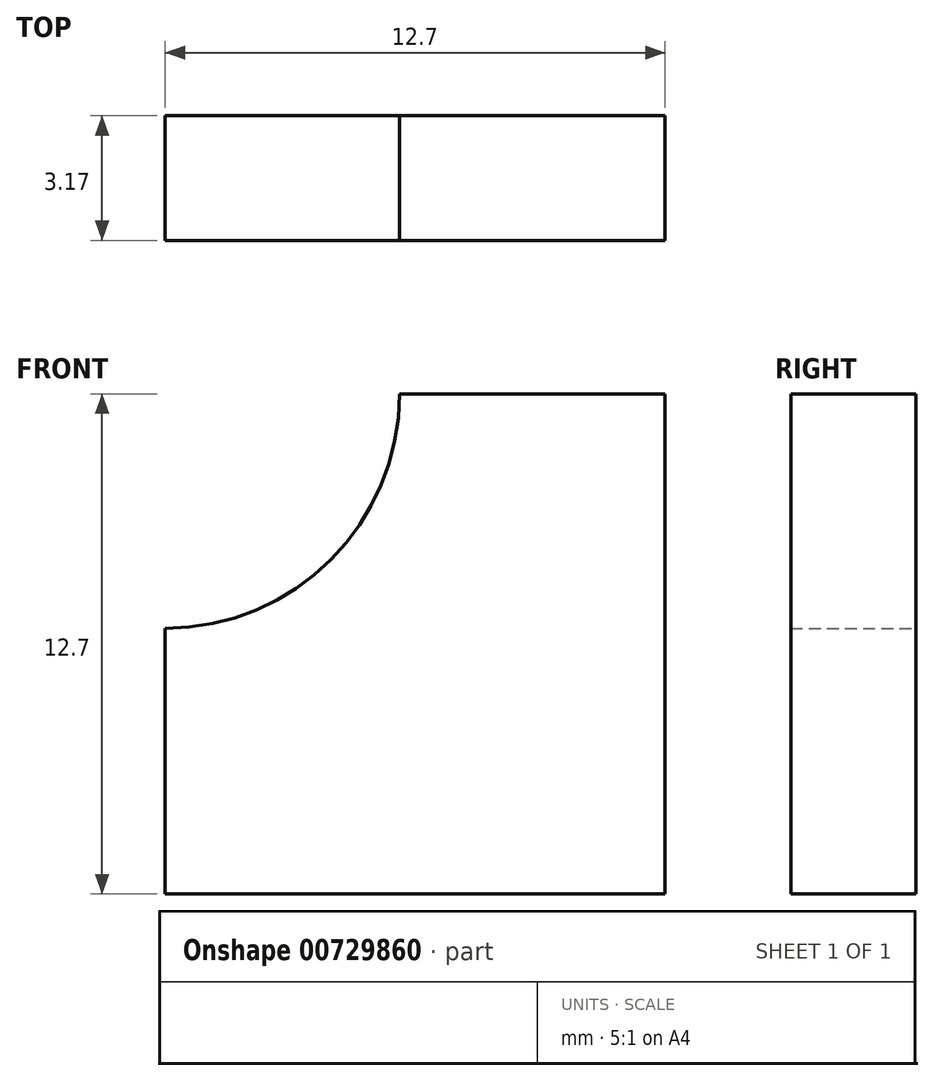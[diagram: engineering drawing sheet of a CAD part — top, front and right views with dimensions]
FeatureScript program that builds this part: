
annotation { "Feature Type Name" : "Feature", "Feature Type Description" : "" }
export const myFeature = defineFeature(function(context is Context, id is Id, definition is map)
    precondition{}
    {
        {
            var Q0;
            Q0=qCreatedBy(makeId("Front.planeOp"),FACE);
            var sketch = newSketch(context, id + "F0", { "sketchPlane" : qUnion([Q0])});
            skLineSegment(sketch, "E0.bottom", {"start": v(-37.74, 10.23) * mm, "end": v(-12.34, 10.23) * mm});
            skLineSegment(sketch, "E0.top", {"start": v(-37.74, -15.17) * mm, "end": v(-12.34, -15.17) * mm});
            skLineSegment(sketch, "E0.left", {"start": v(-37.74, 10.23) * mm, "end": v(-37.74, -15.17) * mm});
            skLineSegment(sketch, "E0.right", {"start": v(-12.34, 10.23) * mm, "end": v(-12.34, -15.17) * mm});
            skLineSegment(sketch, "E1.bottom", {"start": v(-25.04, 10.23) * mm, "end": v(-12.34, 10.23) * mm});
            skLineSegment(sketch, "E1.top", {"start": v(-25.04, -15.17) * mm, "end": v(-12.34, -15.17) * mm});
            skLineSegment(sketch, "E1.left", {"start": v(-25.04, 10.23) * mm, "end": v(-25.04, -15.17) * mm});
            skLineSegment(sketch, "E2.bottom", {"start": v(-12.34, 10.23) * mm, "end": v(-37.74, 10.23) * mm});
            skLineSegment(sketch, "E2.top", {"start": v(-12.34, -2.47) * mm, "end": v(-37.74, -2.47) * mm});
            skLineSegment(sketch, "E2.left", {"start": v(-12.34, 10.23) * mm, "end": v(-12.34, -2.47) * mm});
            skLineSegment(sketch, "E2.right", {"start": v(-37.74, 10.23) * mm, "end": v(-37.74, -2.47) * mm});
            skCircle(sketch, "E3", {"center": v(-25.04, -2.47) * mm, "radius": 5.95 * mm});
            skCircle(sketch, "E4", {"center": v(-31, -2.47) * mm, "radius": 3.97 * mm});
            skSolve(sketch);
        }
        {
            var Q0;
            {var subQ0=sQuery(id+"F0.wireOp",EDGE,"E2.right");Q0=makeQuery(id+"F0.imprint","IMPRINT",FACE,{"disambiguationData":[TD([[makeQuery(id+"F0.imprint","IMPRINT",EDGE,{"derivedFrom":subQ0}),1.0]])]});}
            var Q1;
            {var subQ0=sQuery(id+"F0.wireOp",EDGE,"E2.left");Q1=makeQuery(id+"F0.imprint","IMPRINT",FACE,{"disambiguationData":[TD([[makeQuery(id+"F0.imprint","IMPRINT",EDGE,{"derivedFrom":subQ0}),-1.0]])]});}
            var Q2;
            {var subQ5=sQuery(id+"F0.wireOp",EDGE,"E1.top");Q2=makeQuery(id+"F0.imprint","IMPRINT",FACE,{"disambiguationData":[TD([[makeQuery(id+"F0.imprint","IMPRINT",EDGE,{"derivedFrom":subQ5}),1.0]])]});}
            var Q3;
            {var subQ1=sQuery(id+"F0.wireOp",EDGE,"E0.top");Q3=makeQuery(id+"F0.imprint","IMPRINT",FACE,{"disambiguationData":[TD([[makeQuery(id+"F0.imprint","IMPRINT",EDGE,{"derivedFrom":subQ1}),1.0]])]});}
            extrude(context, id + "F1", {"entities" : qUnion([Q0, Q1, Q2, Q3]), "depth" : 3.17 * mm, "offsetDistance" : 25.4 * mm});
        }
    });
